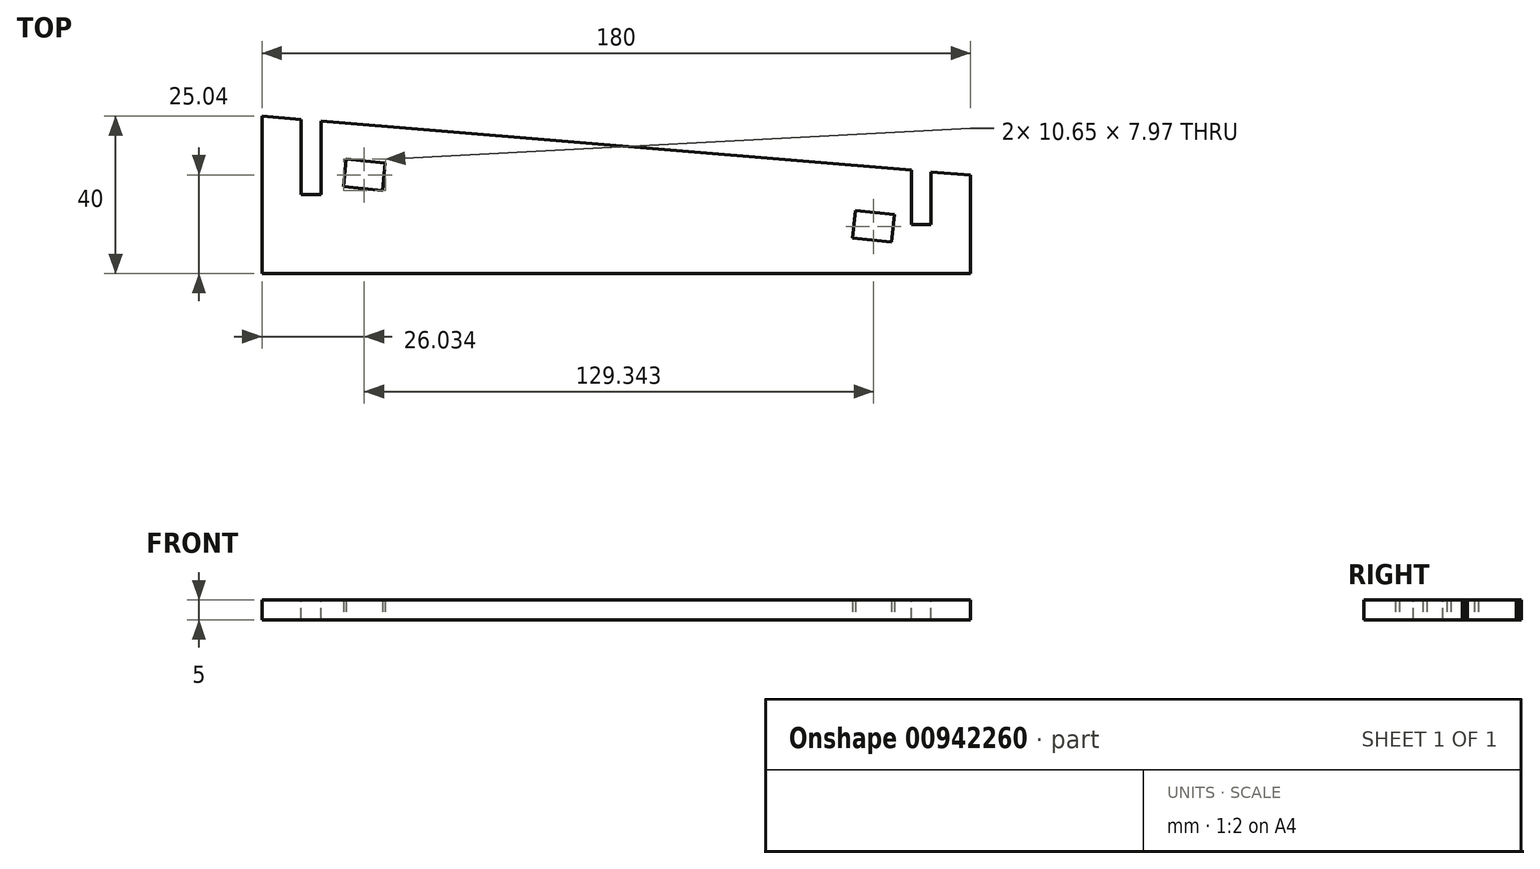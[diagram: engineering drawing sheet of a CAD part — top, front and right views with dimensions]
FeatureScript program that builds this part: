
annotation { "Feature Type Name" : "Feature", "Feature Type Description" : "" }
export const myFeature = defineFeature(function(context is Context, id is Id, definition is map)
    precondition{}
    {
        {
            var Q0;
            Q0=qCreatedBy(makeId("Top.planeOp"),FACE);
            var sketch = newSketch(context, id + "F0", { "sketchPlane" : qUnion([Q0])});
            skLineSegment(sketch, "E0.bottom", {"start": v(-90, 20) * mm, "end": v(90, 20) * mm});
            skLineSegment(sketch, "E0.top", {"start": v(-90, -20) * mm, "end": v(90, -20) * mm});
            skLineSegment(sketch, "E0.left", {"start": v(-90, 20) * mm, "end": v(-90, -20) * mm});
            skLineSegment(sketch, "E0.right", {"start": v(90, 20) * mm, "end": v(90, -20) * mm});
            skSolve(sketch);
        }
        {
            var Q0;
            Q0=makeQuery(id+"F0.imprint","IMPRINT",FACE,{"disambiguationData":[TD([[makeQuery(id+"F0.imprint","IMPRINT",EDGE,{"derivedFrom":sQuery(id+"F0.wireOp",EDGE,"E0.bottom")}),-1.0]])]});
            extrude(context, id + "F1", {"entities" : qUnion([Q0]), "depth" : 5 * mm, "offsetDistance" : 25 * mm});
        }
        {
            var Q0;
            Q0=makeQuery(id+"F1.opExtrude","CAP_FACE",FACE,{"disambiguationData":[OSD([sQuery(id+"F0.wireOp",EDGE,"E0.bottom"),sQuery(id+"F0.wireOp",EDGE,"E0.top"),sQuery(id+"F0.wireOp",EDGE,"E0.left"),sQuery(id+"F0.wireOp",EDGE,"E0.right")])],"isStart":false});
            var sketch = newSketch(context, id + "F2", { "sketchPlane" : qUnion([Q0])});
            skLineSegment(sketch, "E1", {"start": v(-90, 20) * mm, "end": v(90, 20) * mm});
            skLineSegment(sketch, "E2", {"start": v(90, 20) * mm, "end": v(90, 5) * mm});
            skLineSegment(sketch, "E3", {"start": v(90, 5) * mm, "end": v(-90, 20) * mm});
            skSolve(sketch);
        }
        {
            var Q0;
            Q0=makeQuery(id+"F2.imprint","IMPRINT",FACE,{"disambiguationData":[TD([[makeQuery(id+"F2.imprint","IMPRINT",EDGE,{"derivedFrom":sQuery(id+"F2.wireOp",EDGE,"E1")}),-1.0]])]});
            extrude(context, id + "F3", {"entities" : qUnion([Q0]), "operationType" : NewBodyOperationType.REMOVE, "oppositeDirection" : true, "depth" : 25 * mm, "offsetDistance" : 25 * mm});
        }
        {
            var Q0;
            Q0=makeQuery(id+"F1.opExtrude","CAP_FACE",FACE,{"disambiguationData":[OSD([sQuery(id+"F0.wireOp",EDGE,"E0.bottom"),sQuery(id+"F0.wireOp",EDGE,"E0.top"),sQuery(id+"F0.wireOp",EDGE,"E0.left"),sQuery(id+"F0.wireOp",EDGE,"E0.right")])],"isStart":false});
            var sketch = newSketch(context, id + "F4", { "sketchPlane" : qUnion([Q0])});
            skLineSegment(sketch, "E4", {"start": v(-80, 19.17) * mm, "end": v(-80, 0) * mm});
            skLineSegment(sketch, "E5", {"start": v(-80, 0) * mm, "end": v(-75, 0) * mm});
            skLineSegment(sketch, "E6", {"start": v(-75, 0) * mm, "end": v(-75, 18.75) * mm});
            skLineSegment(sketch, "E7", {"start": v(-75, 18.75) * mm, "end": v(-80, 19.17) * mm});
            skLineSegment(sketch, "E8", {"start": v(75, 6.25) * mm, "end": v(75, -7.5) * mm});
            skLineSegment(sketch, "E9", {"start": v(75, -7.5) * mm, "end": v(80, -7.5) * mm});
            skLineSegment(sketch, "E10", {"start": v(80, -7.5) * mm, "end": v(80, 5.83) * mm});
            skLineSegment(sketch, "E11", {"start": v(80, 5.83) * mm, "end": v(75, 6.25) * mm});
            skSolve(sketch);
        }
        {
            var Q0;
            Q0=makeQuery(id+"F4.imprint","IMPRINT",FACE,{"disambiguationData":[TD([[makeQuery(id+"F4.imprint","IMPRINT",EDGE,{"derivedFrom":sQuery(id+"F4.wireOp",EDGE,"E4")}),1.0]])]});
            var Q1;
            Q1=makeQuery(id+"F4.imprint","IMPRINT",FACE,{"disambiguationData":[TD([[makeQuery(id+"F4.imprint","IMPRINT",EDGE,{"derivedFrom":sQuery(id+"F4.wireOp",EDGE,"E8")}),1.0]])]});
            extrude(context, id + "F5", {"entities" : qUnion([Q0, Q1]), "operationType" : NewBodyOperationType.REMOVE, "oppositeDirection" : true, "depth" : 25 * mm, "offsetDistance" : 25 * mm});
        }
        {
            var Q0;
            Q0=makeQuery(id+"F1.opExtrude","CAP_FACE",FACE,{"disambiguationData":[OSD([sQuery(id+"F0.wireOp",EDGE,"E0.bottom"),sQuery(id+"F0.wireOp",EDGE,"E0.top"),sQuery(id+"F0.wireOp",EDGE,"E0.left"),sQuery(id+"F0.wireOp",EDGE,"E0.right")])],"isStart":true});
            var sketch = newSketch(context, id + "F6", { "sketchPlane" : qUnion([Q0])});
            skLineSegment(sketch, "E12.bottom", {"start": v(-69.3, -2.06) * mm, "end": v(-59.34, -1.06) * mm});
            skLineSegment(sketch, "E12.top", {"start": v(-68.59, -9.02) * mm, "end": v(-58.64, -8.02) * mm});
            skLineSegment(sketch, "E12.left", {"start": v(-69.3, -2.06) * mm, "end": v(-68.59, -9.02) * mm});
            skLineSegment(sketch, "E12.right", {"start": v(-59.34, -1.06) * mm, "end": v(-58.64, -8.02) * mm});
            skLineSegment(sketch, "E13.bottom", {"start": v(60.05, 11) * mm, "end": v(70, 12) * mm});
            skLineSegment(sketch, "E13.top", {"start": v(60.75, 4.03) * mm, "end": v(70.7, 5.04) * mm});
            skLineSegment(sketch, "E13.left", {"start": v(60.05, 11) * mm, "end": v(60.75, 4.03) * mm});
            skLineSegment(sketch, "E13.right", {"start": v(70, 12) * mm, "end": v(70.7, 5.04) * mm});
            skSolve(sketch);
        }
        {
            var Q0;
            Q0=makeQuery(id+"F6.imprint","IMPRINT",FACE,{"disambiguationData":[TD([[makeQuery(id+"F6.imprint","IMPRINT",EDGE,{"derivedFrom":sQuery(id+"F6.wireOp",EDGE,"E12.bottom")}),-1.0]])]});
            var Q1;
            Q1=makeQuery(id+"F6.imprint","IMPRINT",FACE,{"disambiguationData":[TD([[makeQuery(id+"F6.imprint","IMPRINT",EDGE,{"derivedFrom":sQuery(id+"F6.wireOp",EDGE,"E13.bottom")}),-1.0]])]});
            extrude(context, id + "F7", {"entities" : qUnion([Q0, Q1]), "operationType" : NewBodyOperationType.REMOVE, "oppositeDirection" : true, "depth" : 25 * mm, "offsetDistance" : 25 * mm});
        }
    });
